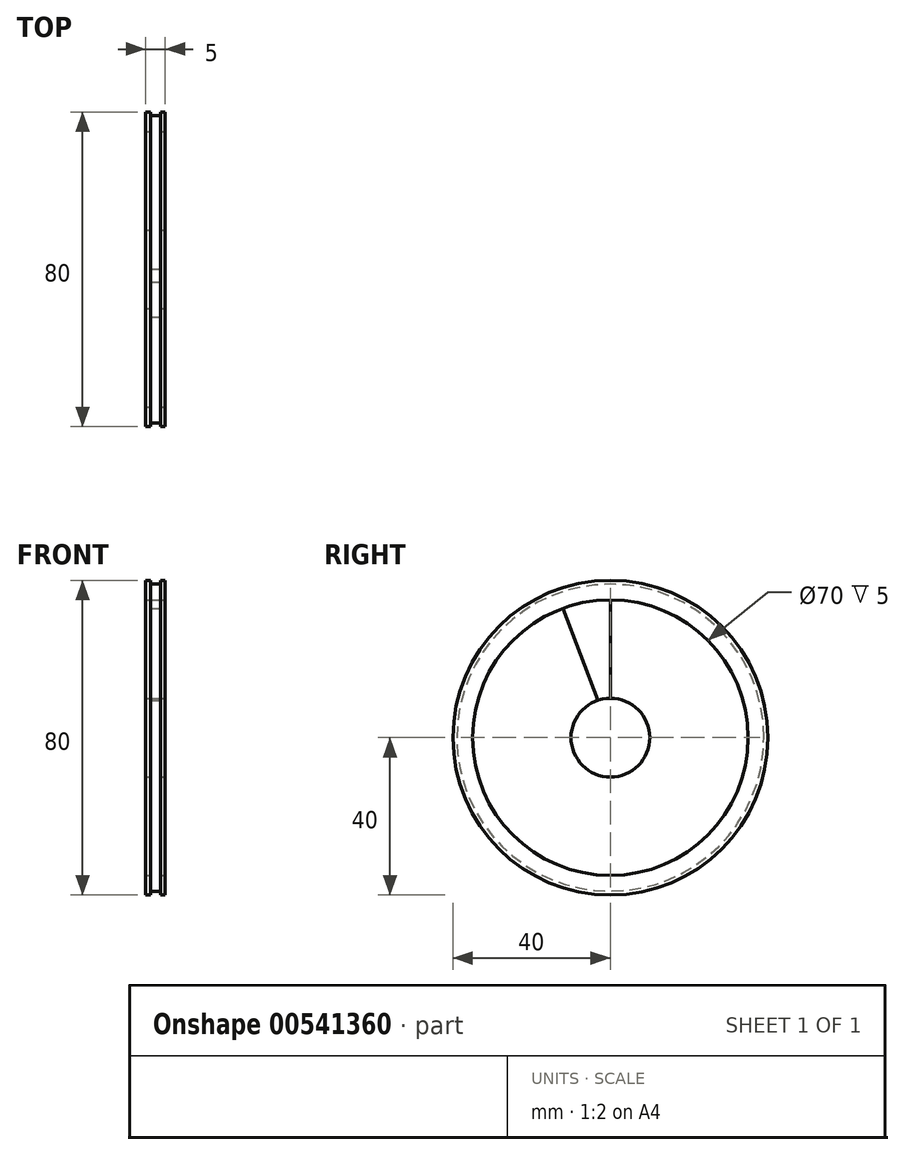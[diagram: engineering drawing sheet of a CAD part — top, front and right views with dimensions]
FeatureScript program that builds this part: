
annotation { "Feature Type Name" : "Feature", "Feature Type Description" : "" }
export const myFeature = defineFeature(function(context is Context, id is Id, definition is map)
    precondition{}
    {
        {
            var Q0;
            Q0=qCreatedBy(makeId("Front.planeOp"),FACE);
            var sketch = newSketch(context, id + "F0", { "sketchPlane" : qUnion([Q0])});
            skLineSegment(sketch, "E0.bottom", {"start": v(0, -20) * mm, "end": v(-5, -20) * mm});
            skLineSegment(sketch, "E0.top", {"start": v(0, 20) * mm, "end": v(-1.25, 20) * mm});
            skLineSegment(sketch, "E0.left", {"start": v(0, -20) * mm, "end": v(0, -10) * mm});
            skLineSegment(sketch, "E0.right", {"start": v(-5, -20) * mm, "end": v(-5, -10) * mm});
            skPoint(sketch, "E1", {"position": v(0, 0) * mm});
            skLineSegment(sketch, "E2.bottom", {"start": v(-5, 15) * mm, "end": v(-3.75, 15) * mm});
            skLineSegment(sketch, "E2.top", {"start": v(-5, -10) * mm, "end": v(-3.75, -10) * mm});
            skLineSegment(sketch, "E2.right", {"start": v(-3.75, 15) * mm, "end": v(-3.75, -10) * mm});
            skLineSegment(sketch, "E3.bottom", {"start": v(0, -10) * mm, "end": v(-1.25, -10) * mm});
            skLineSegment(sketch, "E3.top", {"start": v(0, 15) * mm, "end": v(-1.25, 15) * mm});
            skLineSegment(sketch, "E3.right", {"start": v(-1.25, -10) * mm, "end": v(-1.25, 15) * mm});
            skLineSegment(sketch, "E4.trimOffspring", {"start": v(0, 15) * mm, "end": v(0, 20) * mm});
            skLineSegment(sketch, "E5.trimOffspring", {"start": v(-5, 15) * mm, "end": v(-5, 20) * mm});
            skLineSegment(sketch, "E6.top", {"start": v(-3.75, 19) * mm, "end": v(-1.25, 19) * mm});
            skLineSegment(sketch, "E6.left", {"start": v(-3.75, 20) * mm, "end": v(-3.75, 19) * mm});
            skLineSegment(sketch, "E6.right", {"start": v(-1.25, 20) * mm, "end": v(-1.25, 19) * mm});
            skLineSegment(sketch, "E7.trimOffspring", {"start": v(-3.75, 20) * mm, "end": v(-5, 20) * mm});
            skSolve(sketch);
        }
        {
            var Q0;
            Q0=makeQuery(id+"F0.imprint","IMPRINT",FACE,{"disambiguationData":[TD([[makeQuery(id+"F0.imprint","IMPRINT",EDGE,{"derivedFrom":sQuery(id+"F0.wireOp",EDGE,"E0.bottom")}),-1.0]])]});
            var Q1;
            Q1=sQuery(id+"F0.wireOp",EDGE,"E0.bottom");
            revolve(context, id + "F1", {"entities" : qUnion([Q0]), "axis" : qUnion([Q1]), "revolveType" : RevolveType.FULL});
        }
        {
            var Q0;
            Q0=makeQuery(id+"F1.opRevolve","SWEPT_FACE",FACE,{"disambiguationData":[OSD([sQuery(id+"F0.wireOp",EDGE,"E3.right")])]});
            var sketch = newSketch(context, id + "F2", { "sketchPlane" : qUnion([Q0])});
            skArc(sketch, "E8.0.0", {"start": v(0, 15) * mm, "mid": v(-6.13, 14.46) * mm, "end": v(-12.07, 12.85) * mm});
            skLineSegment(sketch, "E9", {"start": v(0, -10) * mm, "end": v(0, 15) * mm});
            skLineSegment(sketch, "E10", {"start": v(-3.2, -10.52) * mm, "end": v(-12.07, 12.85) * mm});
            skArc(sketch, "E11.0", {"start": v(0, -10) * mm, "mid": v(-1.62, -10.13) * mm, "end": v(-3.2, -10.52) * mm});
            skSolve(sketch);
        }
        {
            var Q0;
            Q0=qSketchRegion(id+"F2",true);
            extrude(context, id + "F3", {"entities" : qUnion([Q0]), "operationType" : NewBodyOperationType.REMOVE, "endBound" : BoundingType.UP_TO_NEXT, "oppositeDirection" : true, "depth" : 25 * mm, "offsetDistance" : 25 * mm});
        }
    });
